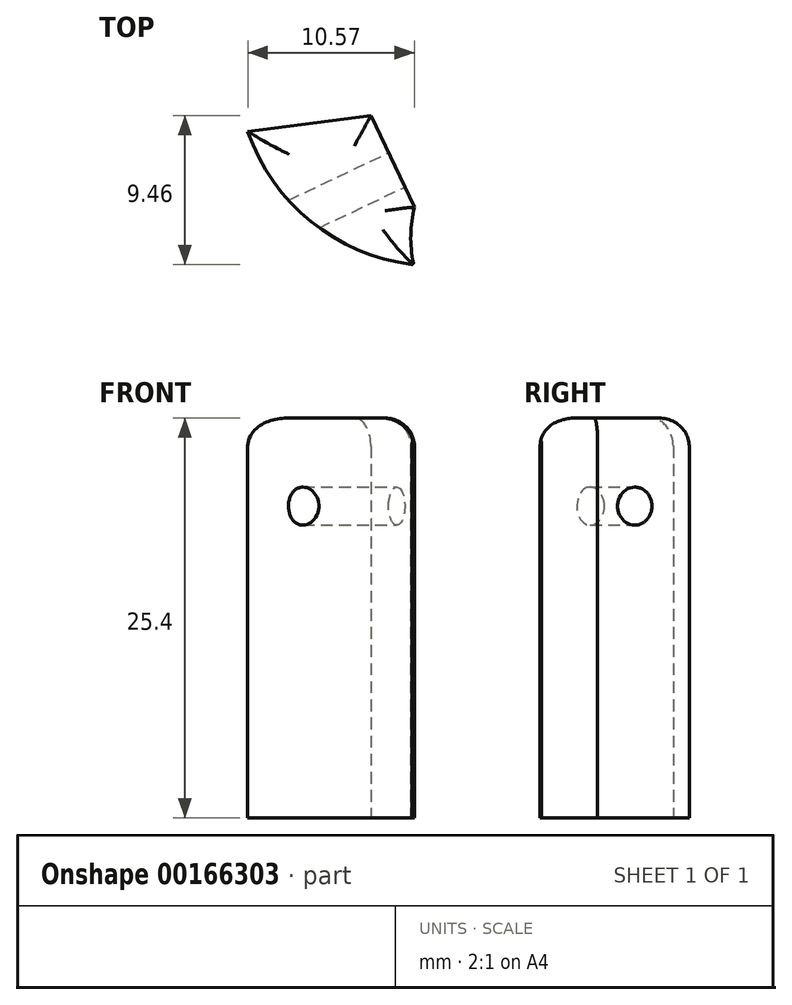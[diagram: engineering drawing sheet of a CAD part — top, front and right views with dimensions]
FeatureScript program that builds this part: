
annotation { "Feature Type Name" : "Feature", "Feature Type Description" : "" }
export const myFeature = defineFeature(function(context is Context, id is Id, definition is map)
    precondition{}
    {
        {
            var Q0;
            Q0=qCreatedBy(makeId("Top.planeOp"),FACE);
            var sketch = newSketch(context, id + "F0", { "sketchPlane" : qUnion([Q0])});
            skCircle(sketch, "E0", {"center": v(0, 0) * mm, "radius": 12.7 * mm});
            skCircle(sketch, "E1.cCircle", {"center": v(-7.9, -9.95) * mm, "radius": 6.27 * mm, "construction": true});
            skLineSegment(sketch, "E1.0", {"start": v(-6.9, -17.64) * mm, "end": v(-14.9, -13.27) * mm});
            skLineSegment(sketch, "E1.1", {"start": v(-14.9, -13.27) * mm, "end": v(-13.22, -4.3) * mm});
            skLineSegment(sketch, "E1.2", {"start": v(-13.22, -4.3) * mm, "end": v(-4.18, -3.14) * mm});
            skLineSegment(sketch, "E1.3", {"start": v(-4.18, -3.14) * mm, "end": v(-0.27, -11.38) * mm});
            skLineSegment(sketch, "E1.4", {"start": v(-0.27, -11.38) * mm, "end": v(-6.9, -17.64) * mm});
            skPoint(sketch, "E1.0.midPoint", {"position": v(-10.9, -15.45) * mm});
            skCircle(sketch, "E2", {"center": v(-12.04, 4.03) * mm, "radius": 14.73 * mm});
            skCircle(sketch, "E3", {"center": v(-0.14, 12.7) * mm, "radius": 9.89 * mm});
            skCircle(sketch, "E4", {"center": v(6.57, -10.87) * mm, "radius": 8.22 * mm});
            skLineSegment(sketch, "E5", {"start": v(22.47, -19.1) * mm, "end": v(-8.66, -19.1) * mm});
            skSolve(sketch);
        }
        {
            var Q0;
            {var subQ0=sQuery(id+"F0.wireOp",EDGE,"E1.2");var subQ1=sQuery(id+"F0.wireOp",EDGE,"E0");var subQ2=makeQuery(id+"F0.imprint","INTERSECT",VERTEX,{"derivedFrom":[subQ1,subQ0]});Q0=makeQuery(id+"F0.imprint","IMPRINT",FACE,{"disambiguationData":[TD([[makeQuery(id+"F0.imprint","IMPRINT",EDGE,{"disambiguationData":[TD([[subQ2,-1.0]])],"derivedFrom":subQ1}),1.0]])]});}
            var Q1;
            {var subQ0=sQuery(id+"F0.wireOp",EDGE,"E1.4");var subQ1=sQuery(id+"F0.wireOp",EDGE,"E0");var subQ2=makeQuery(id+"F0.imprint","INTERSECT",VERTEX,{"derivedFrom":[subQ1,subQ0]});Q1=makeQuery(id+"F0.imprint","IMPRINT",FACE,{"disambiguationData":[TD([[makeQuery(id+"F0.imprint","IMPRINT",EDGE,{"disambiguationData":[TD([[subQ2,1.0]])],"derivedFrom":subQ1}),1.0]])]});}
            extrude(context, id + "F1", {"entities" : qUnion([Q0, Q1]), "depth" : 25.4 * mm});
        }
        {
            var Q0;
            Q0=makeQuery(id+"F1.opExtrude","CAP_EDGE",EDGE,{"disambiguationData":[OSD([sQuery(id+"F0.wireOp",EDGE,"E4")])],"isStart":false});
            var Q1;
            Q1=makeQuery(id+"F1.opExtrude","CAP_EDGE",EDGE,{"disambiguationData":[OSD([sQuery(id+"F0.wireOp",EDGE,"E1.3")])],"isStart":false});
            var Q2;
            Q2=makeQuery(id+"F1.opExtrude","CAP_EDGE",EDGE,{"disambiguationData":[OSD([sQuery(id+"F0.wireOp",EDGE,"E1.2")])],"isStart":false});
            var Q3;
            Q3=makeQuery(id+"F1.opExtrude","CAP_EDGE",EDGE,{"disambiguationData":[OSD([sQuery(id+"F0.wireOp",EDGE,"E0")])],"isStart":false});
            fillet(context, id + "F2", {"entities" : qUnion([Q0, Q1, Q2, Q3]), "radius" : 1.78 * mm, "tangentPropagation" : true, "allowEdgeOverflow" : false});
        }
        {
            var Q0;
            Q0=makeQuery(id+"F1.opExtrude","SWEPT_FACE",FACE,{"disambiguationData":[OSD([sQuery(id+"F0.wireOp",EDGE,"E1.3")])]});
            var sketch = newSketch(context, id + "F3", { "sketchPlane" : qUnion([Q0])});
            skCircle(sketch, "E6", {"center": v(-4.87, 19.8) * mm, "radius": 1.2 * mm});
            skSolve(sketch);
        }
        {
            var Q0;
            Q0=makeQuery(id+"F3.imprint","IMPRINT",FACE,{"disambiguationData":[TD([[makeQuery(id+"F3.imprint","IMPRINT",EDGE,{"derivedFrom":sQuery(id+"F3.wireOp",EDGE,"E6")}),1.0]])]});
            extrude(context, id + "F4", {"entities" : qUnion([Q0]), "operationType" : NewBodyOperationType.REMOVE, "oppositeDirection" : true, "depth" : 25.4 * mm});
        }
    });
